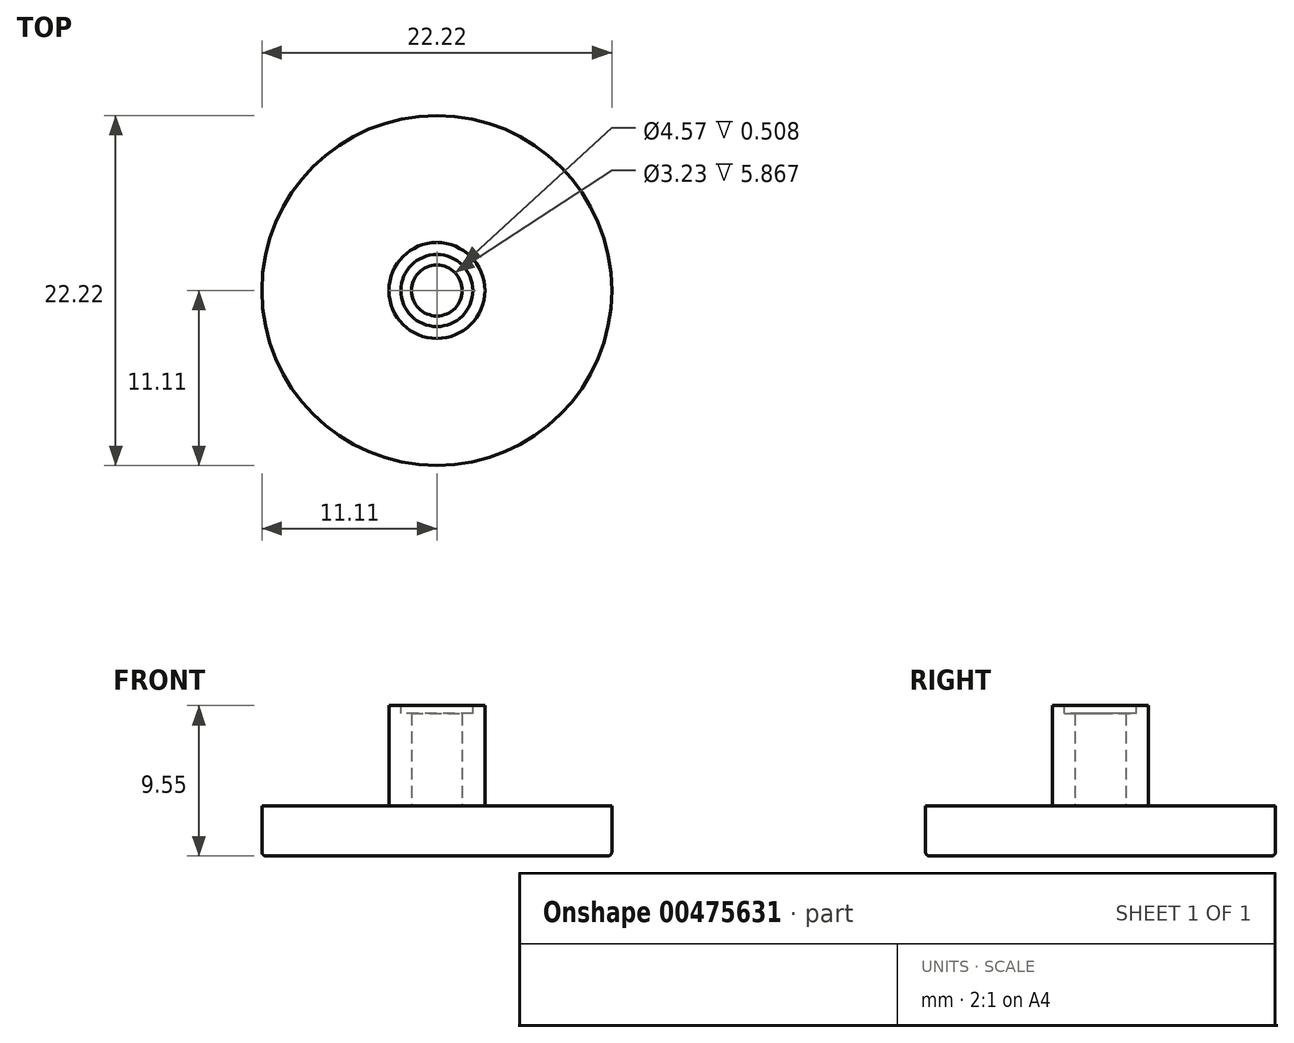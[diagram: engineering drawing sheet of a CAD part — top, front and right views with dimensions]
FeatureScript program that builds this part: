
annotation { "Feature Type Name" : "Feature", "Feature Type Description" : "" }
export const myFeature = defineFeature(function(context is Context, id is Id, definition is map)
    precondition{}
    {
        {
            var Q0;
            Q0=qCreatedBy(makeId("Top.planeOp"),FACE);
            var sketch = newSketch(context, id + "F0", { "sketchPlane" : qUnion([Q0])});
            skCircle(sketch, "E0", {"center": v(0, 0) * mm, "radius": 11.11 * mm});
            skCircle(sketch, "E1", {"center": v(0, 0) * mm, "radius": 3.05 * mm});
            skCircle(sketch, "E2", {"center": v(0, 0) * mm, "radius": 1.61 * mm});
            skSolve(sketch);
        }
        {
            var Q0;
            Q0=qSketchRegion(id+"F0",true);
            extrude(context, id + "F1", {"entities" : qUnion([Q0]), "depth" : 3.17 * mm});
        }
        {
            var Q0;
            Q0=qCreatedBy(makeId("Top.planeOp"),FACE);
            var sketch = newSketch(context, id + "F2", { "sketchPlane" : qUnion([Q0])});
            skCircle(sketch, "E3", {"center": v(0, 0) * mm, "radius": 1.61 * mm});
            skSolve(sketch);
        }
        {
            var Q0;
            Q0=makeQuery(id+"F1.opExtrude","CAP_FACE",FACE,{"disambiguationData":[OSD([sQuery(id+"F0.wireOp",EDGE,"E0"),sQuery(id+"F0.wireOp",EDGE,"E1")])],"isStart":true});
            var sketch = newSketch(context, id + "F3", { "sketchPlane" : qUnion([Q0])});
            skCircle(sketch, "E4", {"center": v(0, 0) * mm, "radius": 3.05 * mm});
            skSolve(sketch);
        }
        {
            var Q0;
            Q0=qSketchRegion(id+"F3",true);
            extrude(context, id + "F4", {"entities" : qUnion([Q0]), "operationType" : NewBodyOperationType.ADD, "oppositeDirection" : true, "depth" : 9.55 * mm});
        }
        {
            var Q0;
            Q0=makeQuery(id+"F2.imprint","IMPRINT",FACE,{"disambiguationData":[TD([[makeQuery(id+"F2.imprint","IMPRINT",EDGE,{"derivedFrom":sQuery(id+"F2.wireOp",EDGE,"E3")}),1.0]])]});
            extrude(context, id + "F5", {"entities" : qUnion([Q0]), "operationType" : NewBodyOperationType.REMOVE, "depth" : 25.4 * mm});
        }
        {
            var Q0;
            Q0=makeQuery(id+"F4.boolean.opBoolean","MERGE",FACE,{"derivedFrom":[makeQuery(id+"F1.opExtrude","CAP_FACE",FACE,{"disambiguationData":[OSD([sQuery(id+"F0.wireOp",EDGE,"E0"),sQuery(id+"F0.wireOp",EDGE,"E1")])],"isStart":true}),makeQuery(id+"F4.opExtrude","CAP_FACE",FACE,{"disambiguationData":[OSD([sQuery(id+"F3.wireOp",EDGE,"E4")])],"isStart":true})]});
            var sketch = newSketch(context, id + "F6", { "sketchPlane" : qUnion([Q0])});
            skCircle(sketch, "E5", {"center": v(0, 0) * mm, "radius": 1.61 * mm});
            skSolve(sketch);
        }
        {
            var Q0;
            Q0=qSketchRegion(id+"F6",true);
            extrude(context, id + "F7", {"entities" : qUnion([Q0]), "operationType" : NewBodyOperationType.ADD, "oppositeDirection" : true, "depth" : 3.17 * mm});
        }
        {
            var Q0;
            Q0=makeQuery(id+"F4.opExtrude","CAP_FACE",FACE,{"disambiguationData":[OSD([sQuery(id+"F3.wireOp",EDGE,"E4")])],"isStart":false});
            var sketch = newSketch(context, id + "F8", { "sketchPlane" : qUnion([Q0])});
            skArc(sketch, "E6", {"start": v(-2.29, 0) * mm, "mid": v(0, -2.29) * mm, "end": v(2.29, 0) * mm});
            skArc(sketch, "E7", {"start": v(2.29, 0) * mm, "mid": v(0, 2.29) * mm, "end": v(-2.29, 0) * mm});
            skSolve(sketch);
        }
        {
            var Q0;
            Q0=makeQuery(id+"F8.imprint","IMPRINT",FACE,{"disambiguationData":[TD([[makeQuery(id+"F8.imprint","IMPRINT",EDGE,{"derivedFrom":sQuery(id+"F8.wireOp",EDGE,"E6")}),1.0]])]});
            extrude(context, id + "F9", {"entities" : qUnion([Q0]), "operationType" : NewBodyOperationType.REMOVE, "oppositeDirection" : true, "depth" : 0.5 * mm});
        }
        {
            var Q0;
            Q0=makeQuery(id+"F1.opExtrude","CAP_EDGE",EDGE,{"disambiguationData":[OSD([sQuery(id+"F0.wireOp",EDGE,"E0")])],"isStart":true});
            fillet(context, id + "F10", {"entities" : qUnion([Q0]), "radius" : 0.25 * mm, "tangentPropagation" : true, "allowEdgeOverflow" : false});
        }
    });
